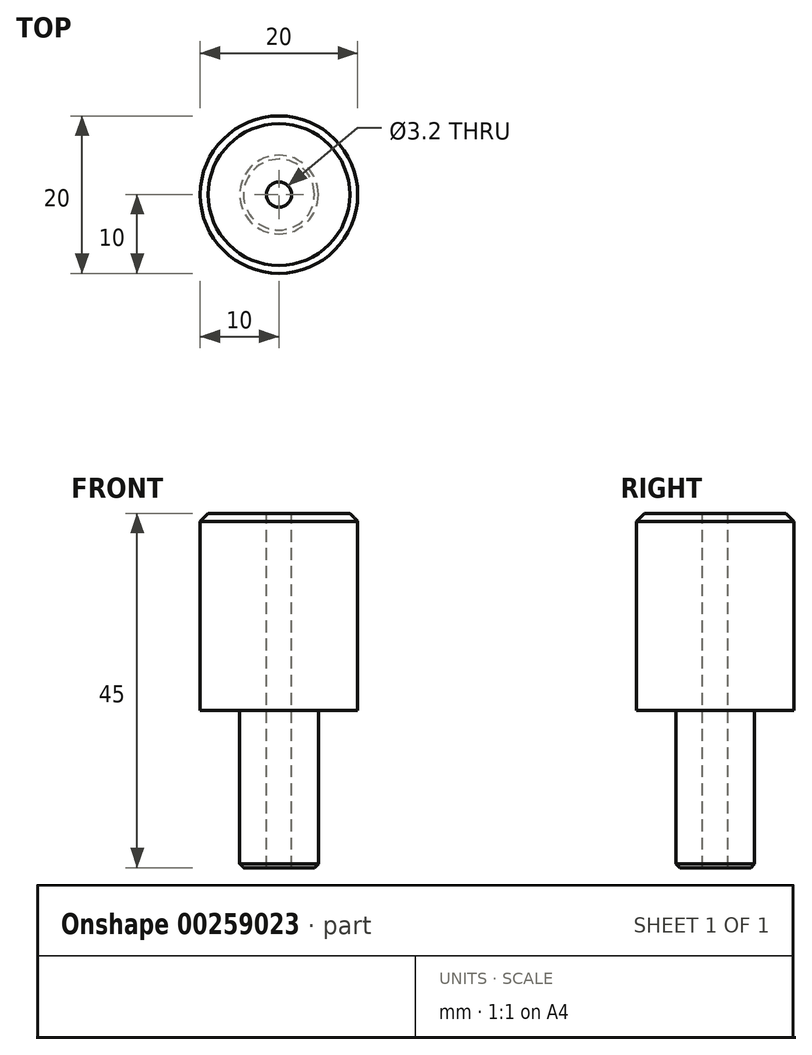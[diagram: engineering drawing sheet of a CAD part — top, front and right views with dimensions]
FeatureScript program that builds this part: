
annotation { "Feature Type Name" : "Feature", "Feature Type Description" : "" }
export const myFeature = defineFeature(function(context is Context, id is Id, definition is map)
    precondition{}
    {
        {
            var Q0;
            Q0=qCreatedBy(makeId("Top.planeOp"),FACE);
            var sketch = newSketch(context, id + "F0", { "sketchPlane" : qUnion([Q0])});
            skCircle(sketch, "E0", {"center": v(0, 0) * mm, "radius": 10 * mm});
            skSolve(sketch);
        }
        {
            var Q0;
            Q0=makeQuery(id+"F0.imprint","IMPRINT",FACE,{"disambiguationData":[TD([[makeQuery(id+"F0.imprint","IMPRINT",EDGE,{"derivedFrom":sQuery(id+"F0.wireOp",EDGE,"E0")}),1.0]])]});
            extrude(context, id + "F1", {"entities" : qUnion([Q0]), "depth" : 25 * mm, "offsetDistance" : 25 * mm});
        }
        {
            var Q0;
            Q0=makeQuery(id+"F1.opExtrude","CAP_EDGE",EDGE,{"disambiguationData":[OSD([sQuery(id+"F0.wireOp",EDGE,"E0")])],"isStart":false});
            chamfer(context, id + "F2", {"entities" : qUnion([Q0]), "width" : 1 * mm, "tangentPropagation" : true});
        }
        {
            var Q0;
            Q0=makeQuery(id+"F1.opExtrude","CAP_FACE",FACE,{"disambiguationData":[OSD([sQuery(id+"F0.wireOp",EDGE,"E0")])],"isStart":true});
            var sketch = newSketch(context, id + "F3", { "sketchPlane" : qUnion([Q0])});
            skCircle(sketch, "E1", {"center": v(0, 0) * mm, "radius": 5 * mm});
            skSolve(sketch);
        }
        {
            var Q0;
            Q0=makeQuery(id+"F3.imprint","IMPRINT",FACE,{"disambiguationData":[TD([[makeQuery(id+"F3.imprint","IMPRINT",EDGE,{"derivedFrom":sQuery(id+"F3.wireOp",EDGE,"E1")}),1.0]])]});
            extrude(context, id + "F4", {"entities" : qUnion([Q0]), "operationType" : NewBodyOperationType.ADD, "depth" : 20 * mm, "offsetDistance" : 25 * mm});
        }
        {
            var Q0;
            Q0=makeQuery(id+"F4.opExtrude","CAP_EDGE",EDGE,{"disambiguationData":[OSD([sQuery(id+"F3.wireOp",EDGE,"E1")])],"isStart":false});
            chamfer(context, id + "F5", {"entities" : qUnion([Q0]), "width" : 0.5 * mm, "tangentPropagation" : true});
        }
        {
            var Q0;
            Q0=makeQuery(id+"F1.opExtrude","CAP_FACE",FACE,{"disambiguationData":[OSD([sQuery(id+"F0.wireOp",EDGE,"E0")])],"isStart":false});
            var sketch = newSketch(context, id + "F6", { "sketchPlane" : qUnion([Q0])});
            skCircle(sketch, "E2", {"center": v(0, 0) * mm, "radius": 1.6 * mm});
            skSolve(sketch);
        }
        {
            var Q0;
            Q0=makeQuery(id+"F6.imprint","IMPRINT",FACE,{"disambiguationData":[TD([[makeQuery(id+"F6.imprint","IMPRINT",EDGE,{"derivedFrom":sQuery(id+"F6.wireOp",EDGE,"E2")}),1.0]])]});
            extrude(context, id + "F7", {"entities" : qUnion([Q0]), "operationType" : NewBodyOperationType.REMOVE, "endBound" : BoundingType.THROUGH_ALL, "oppositeDirection" : true, "depth" : 25 * mm, "offsetDistance" : 25 * mm});
        }
    });
